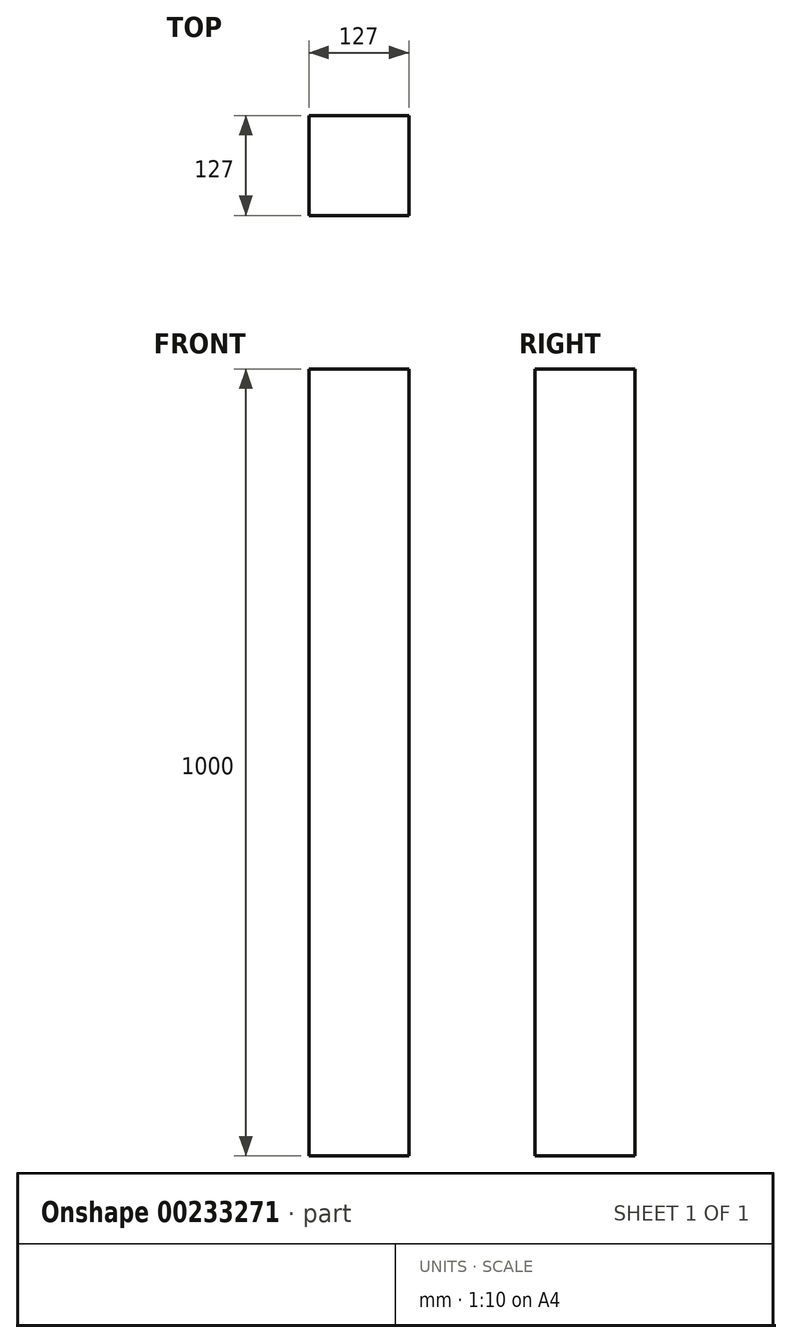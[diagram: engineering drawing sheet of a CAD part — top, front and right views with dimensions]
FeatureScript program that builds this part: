
annotation { "Feature Type Name" : "Feature", "Feature Type Description" : "" }
export const myFeature = defineFeature(function(context is Context, id is Id, definition is map)
    precondition{}
    {
        {
            var Q0;
            Q0=qCreatedBy(makeId("Front.planeOp"),FACE);
            var sketch = newSketch(context, id + "F0", { "sketchPlane" : qUnion([Q0])});
            skLineSegment(sketch, "E0.bottom", {"start": v(-95.66, 762.64) * mm, "end": v(31.34, 762.64) * mm});
            skLineSegment(sketch, "E0.top", {"start": v(-95.66, -237.36) * mm, "end": v(31.34, -237.36) * mm});
            skLineSegment(sketch, "E0.left", {"start": v(-95.66, 762.64) * mm, "end": v(-95.66, -237.36) * mm});
            skLineSegment(sketch, "E0.right", {"start": v(31.34, 762.64) * mm, "end": v(31.34, -237.36) * mm});
            skSolve(sketch);
        }
        {
            var Q0;
            Q0 = qSketchRegion(id + "F0", true);
            extrude(context, id + "F1", {"entities" : qUnion([Q0]), "depth" : 127 * mm});
        }
    });
